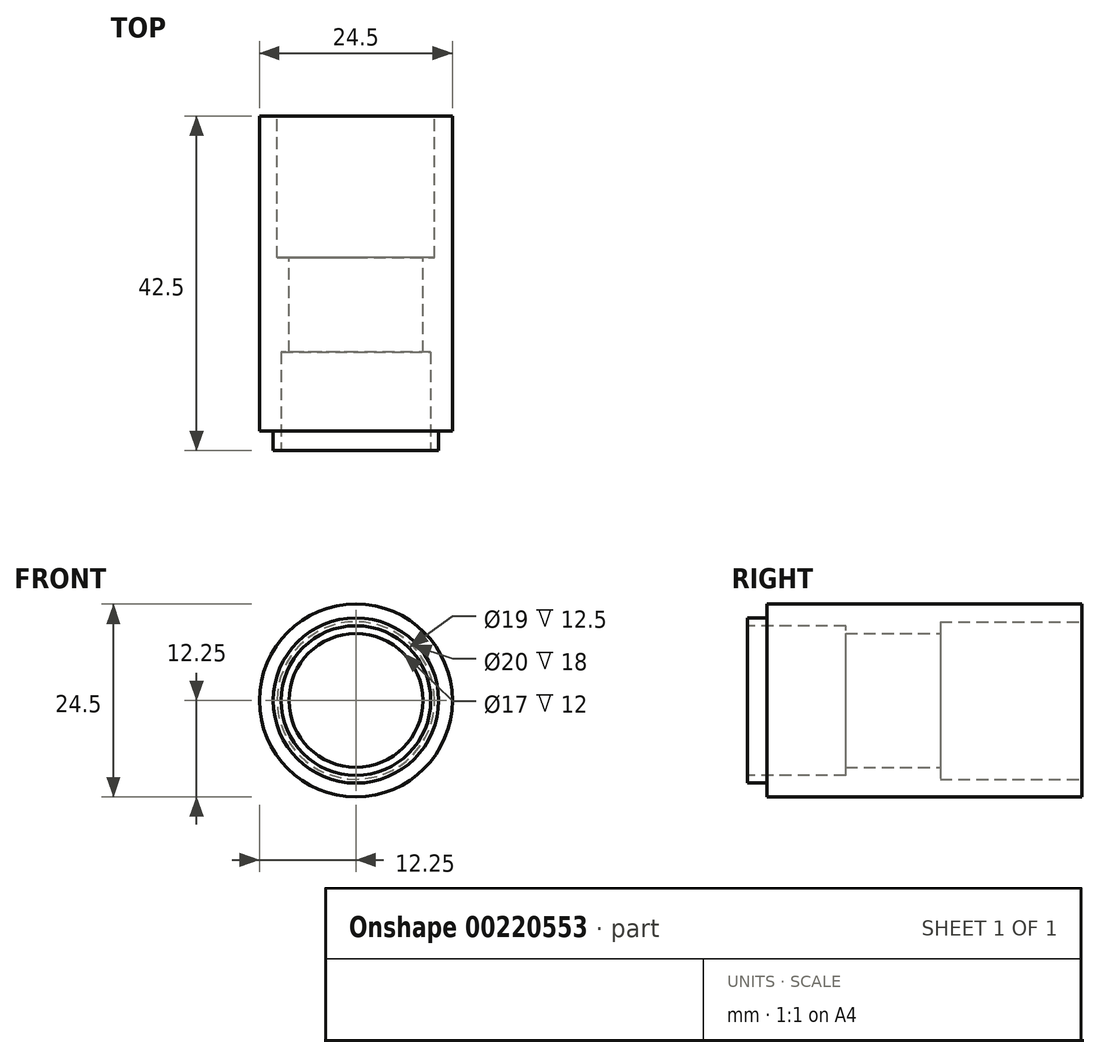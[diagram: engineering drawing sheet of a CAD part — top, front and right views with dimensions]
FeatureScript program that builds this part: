
annotation { "Feature Type Name" : "Feature", "Feature Type Description" : "" }
export const myFeature = defineFeature(function(context is Context, id is Id, definition is map)
    precondition{}
    {
        {
            var Q0;
            Q0=qCreatedBy(makeId("Front.planeOp"),FACE);
            var sketch = newSketch(context, id + "F0", { "sketchPlane" : qUnion([Q0])});
            skCircle(sketch, "E0", {"center": v(0, 0) * mm, "radius": 12.25 * mm});
            skSolve(sketch);
        }
        {
            var Q0;
            Q0=makeQuery(id+"F0.imprint","IMPRINT",FACE,{"disambiguationData":[TD([[makeQuery(id+"F0.imprint","IMPRINT",EDGE,{"derivedFrom":sQuery(id+"F0.wireOp",EDGE,"E0")}),1.0]])]});
            extrude(context, id + "F1", {"entities" : qUnion([Q0]), "depth" : 42.5 * mm});
        }
        {
            var Q0;
            Q0=makeQuery(id+"F1.opExtrude","CAP_FACE",FACE,{"disambiguationData":[OSD([sQuery(id+"F0.wireOp",EDGE,"E0")])],"isStart":false});
            var sketch = newSketch(context, id + "F2", { "sketchPlane" : qUnion([Q0])});
            skCircle(sketch, "E1", {"center": v(0, 0) * mm, "radius": 10.5 * mm});
            skSolve(sketch);
        }
        {
            var Q0;
            Q0=makeQuery(id+"F2.imprint","IMPRINT",FACE,{"disambiguationData":[TD([[makeQuery(id+"F2.imprint","IMPRINT",EDGE,{"derivedFrom":sQuery(id+"F2.wireOp",EDGE,"E1")}),-1.0]])]});
            extrude(context, id + "F3", {"entities" : qUnion([Q0]), "operationType" : NewBodyOperationType.REMOVE, "oppositeDirection" : true, "depth" : 2.5 * mm});
        }
        {
            var Q0;
            Q0=makeQuery(id+"F1.opExtrude","CAP_FACE",FACE,{"disambiguationData":[OSD([sQuery(id+"F0.wireOp",EDGE,"E0")])],"isStart":false});
            var sketch = newSketch(context, id + "F4", { "sketchPlane" : qUnion([Q0])});
            skCircle(sketch, "E2", {"center": v(0, 0) * mm, "radius": 9.5 * mm});
            skSolve(sketch);
        }
        {
            var Q0;
            Q0=makeQuery(id+"F4.imprint","IMPRINT",FACE,{"disambiguationData":[TD([[makeQuery(id+"F4.imprint","IMPRINT",EDGE,{"derivedFrom":sQuery(id+"F4.wireOp",EDGE,"E2")}),1.0]])]});
            extrude(context, id + "F5", {"entities" : qUnion([Q0]), "operationType" : NewBodyOperationType.REMOVE, "oppositeDirection" : true, "depth" : 12.5 * mm});
        }
        {
            var Q0;
            Q0=makeQuery(id+"F1.opExtrude","CAP_FACE",FACE,{"disambiguationData":[OSD([sQuery(id+"F0.wireOp",EDGE,"E0")])],"isStart":true});
            var sketch = newSketch(context, id + "F6", { "sketchPlane" : qUnion([Q0])});
            skCircle(sketch, "E3", {"center": v(0, 0) * mm, "radius": 10 * mm});
            skSolve(sketch);
        }
        {
            var Q0;
            Q0=makeQuery(id+"F6.imprint","IMPRINT",FACE,{"disambiguationData":[TD([[makeQuery(id+"F6.imprint","IMPRINT",EDGE,{"derivedFrom":sQuery(id+"F6.wireOp",EDGE,"E3")}),1.0]])]});
            extrude(context, id + "F7", {"entities" : qUnion([Q0]), "operationType" : NewBodyOperationType.REMOVE, "oppositeDirection" : true, "depth" : 18 * mm});
        }
        {
            var Q0;
            Q0=makeQuery(id+"F7.boolean.opBoolean","COPY",FACE,{"derivedFrom":makeQuery(id+"F7.opExtrude","CAP_FACE",FACE,{"disambiguationData":[OSD([sQuery(id+"F6.wireOp",EDGE,"E3")])],"isStart":false})});
            var sketch = newSketch(context, id + "F8", { "sketchPlane" : qUnion([Q0])});
            skCircle(sketch, "E4", {"center": v(0, 0) * mm, "radius": 8.5 * mm});
            skSolve(sketch);
        }
        {
            var Q0;
            Q0=makeQuery(id+"F8.imprint","IMPRINT",FACE,{"disambiguationData":[TD([[makeQuery(id+"F8.imprint","IMPRINT",EDGE,{"derivedFrom":sQuery(id+"F8.wireOp",EDGE,"E4")}),1.0]])]});
            extrude(context, id + "F9", {"entities" : qUnion([Q0]), "operationType" : NewBodyOperationType.REMOVE, "oppositeDirection" : true, "depth" : 25 * mm});
        }
    });
